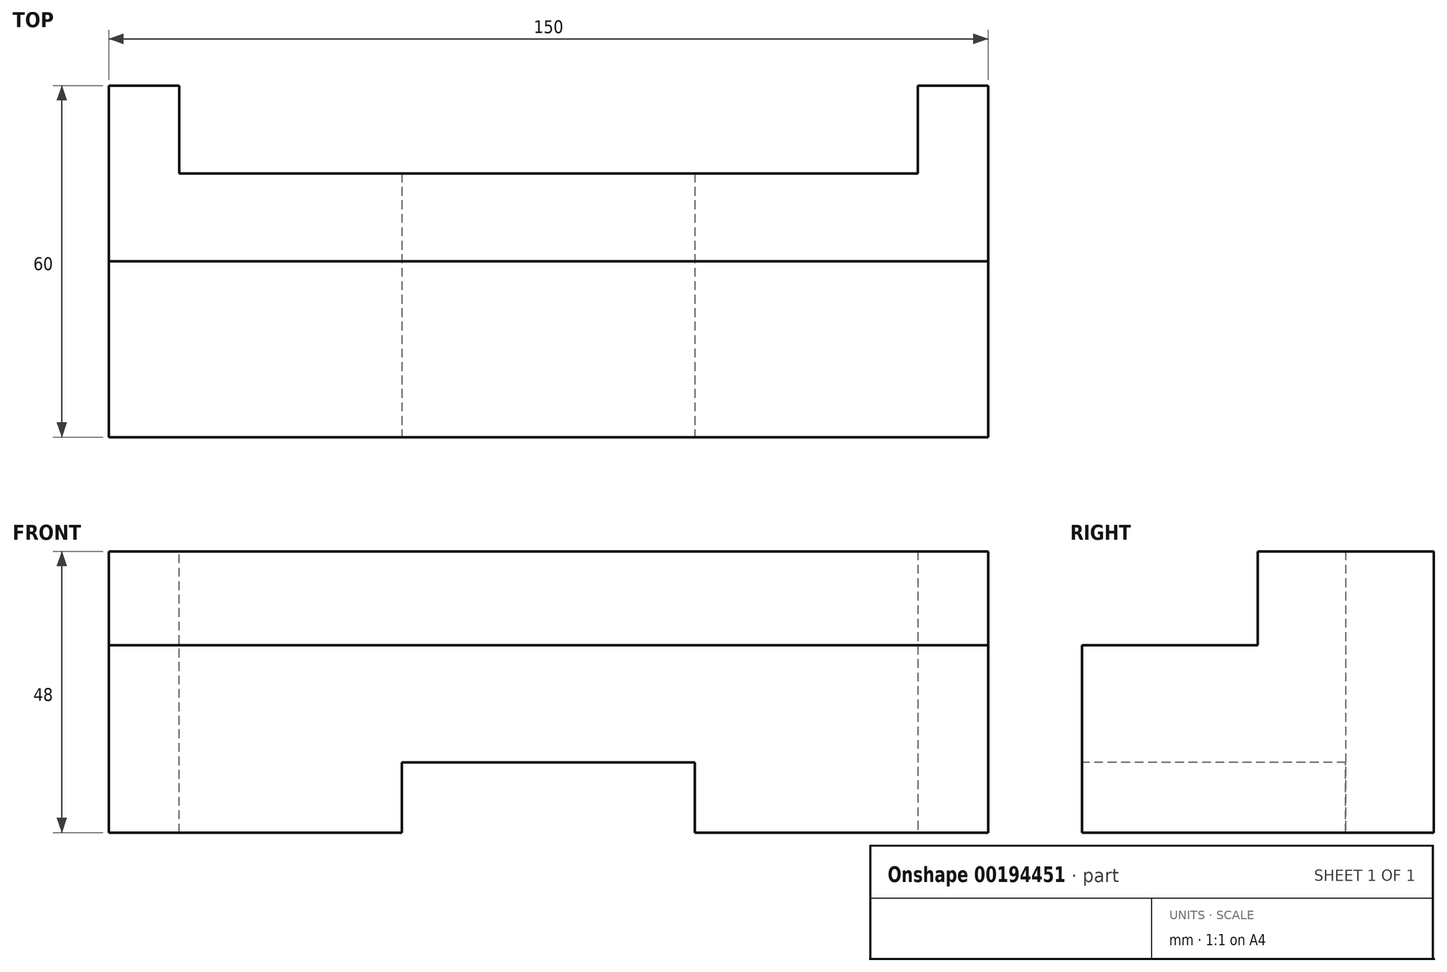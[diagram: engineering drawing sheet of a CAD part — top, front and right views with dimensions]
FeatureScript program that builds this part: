
annotation { "Feature Type Name" : "Feature", "Feature Type Description" : "" }
export const myFeature = defineFeature(function(context is Context, id is Id, definition is map)
    precondition{}
    {
        {
            var Q0;
            Q0=qCreatedBy(makeId("Right.planeOp"),FACE);
            var sketch = newSketch(context, id + "F0", { "sketchPlane" : qUnion([Q0])});
            skLineSegment(sketch, "E0", {"start": v(0, 0) * mm, "end": v(60, 0) * mm});
            skLineSegment(sketch, "E1", {"start": v(60, 0) * mm, "end": v(60, 48) * mm});
            skLineSegment(sketch, "E2", {"start": v(60, 48) * mm, "end": v(30, 48) * mm});
            skLineSegment(sketch, "E3", {"start": v(30, 48) * mm, "end": v(30, 32) * mm});
            skLineSegment(sketch, "E4", {"start": v(30, 32) * mm, "end": v(0, 32) * mm});
            skLineSegment(sketch, "E5", {"start": v(0, 32) * mm, "end": v(0, 0) * mm});
            skSolve(sketch);
        }
        {
            var Q0;
            Q0=makeQuery(id+"F0.imprint","IMPRINT",FACE,{"disambiguationData":[TD([[makeQuery(id+"F0.imprint","IMPRINT",EDGE,{"derivedFrom":sQuery(id+"F0.wireOp",EDGE,"E0")}),1.0]])]});
            extrude(context, id + "F1", {"entities" : qUnion([Q0]), "depth" : 150 * mm});
        }
        {
            var Q0;
            Q0=qCreatedBy(makeId("Front.planeOp"),FACE);
            var sketch = newSketch(context, id + "F2", { "sketchPlane" : qUnion([Q0])});
            skLineSegment(sketch, "E6", {"start": v(50, 0) * mm, "end": v(50, 12) * mm});
            skLineSegment(sketch, "E7", {"start": v(50, 12) * mm, "end": v(100, 12) * mm});
            skLineSegment(sketch, "E8", {"start": v(100, 12) * mm, "end": v(100, 0) * mm});
            skLineSegment(sketch, "E9", {"start": v(50, 0) * mm, "end": v(100, 0) * mm});
            skSolve(sketch);
        }
        {
            var Q0;
            Q0 = qSketchRegion(id + "F2", true);
            extrude(context, id + "F3", {"entities" : qUnion([Q0]), "operationType" : NewBodyOperationType.REMOVE, "oppositeDirection" : true, "depth" : 60 * mm});
        }
        {
            var Q0;
            Q0=qCreatedBy(makeId("Top.planeOp"),FACE);
            var sketch = newSketch(context, id + "F4", { "sketchPlane" : qUnion([Q0])});
            skLineSegment(sketch, "E10", {"start": v(12, 60.08) * mm, "end": v(12, 45) * mm});
            skLineSegment(sketch, "E11", {"start": v(12, 45) * mm, "end": v(138, 45) * mm});
            skLineSegment(sketch, "E12", {"start": v(138, 45) * mm, "end": v(138, 60.08) * mm});
            skLineSegment(sketch, "E13", {"start": v(138, 60.08) * mm, "end": v(12, 60.08) * mm});
            skSolve(sketch);
        }
        {
            var Q0;
            Q0 = qSketchRegion(id + "F4", true);
            var Q1;
            Q1=sQuery(id+"F4.wireOp",EDGE,"E11");
            extrude(context, id + "F5", {"entities" : qUnion([Q0]), "operationType" : NewBodyOperationType.REMOVE, "surfaceEntities" : qUnion([Q1]), "depth" : 48 * mm});
        }
    });
